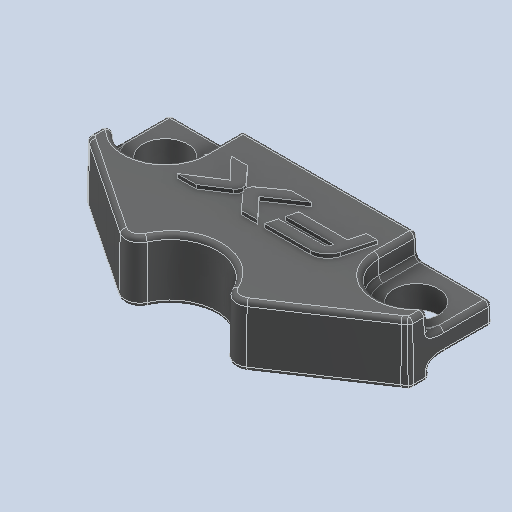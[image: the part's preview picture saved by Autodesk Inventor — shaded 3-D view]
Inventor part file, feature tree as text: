
AUTODESK INVENTOR PART (.ipt)
format: ipt  version: 2024.2 (Build 282272000, 272)  size: 431,104 bytes
history: native  units: in
note: dims shown in document units (in); Inventor stores cm internally (conversion verified against a paired STEP export)
features: fillet x1
ambient origin geometry x8: Origin, YZ Plane, XZ Plane, XY Plane, X Axis, Y Axis, Z Axis, Center Point
bodies: Solid1 (feature_tree)
feature tree (1):
  fillet  "Fillet3"  [1 undecoded]
note: 1 required parameter value undecoded (feature->parameter linkage not recoverable at this tier; creation-order binding heuristic only, values carry confidence <= 0.55)
